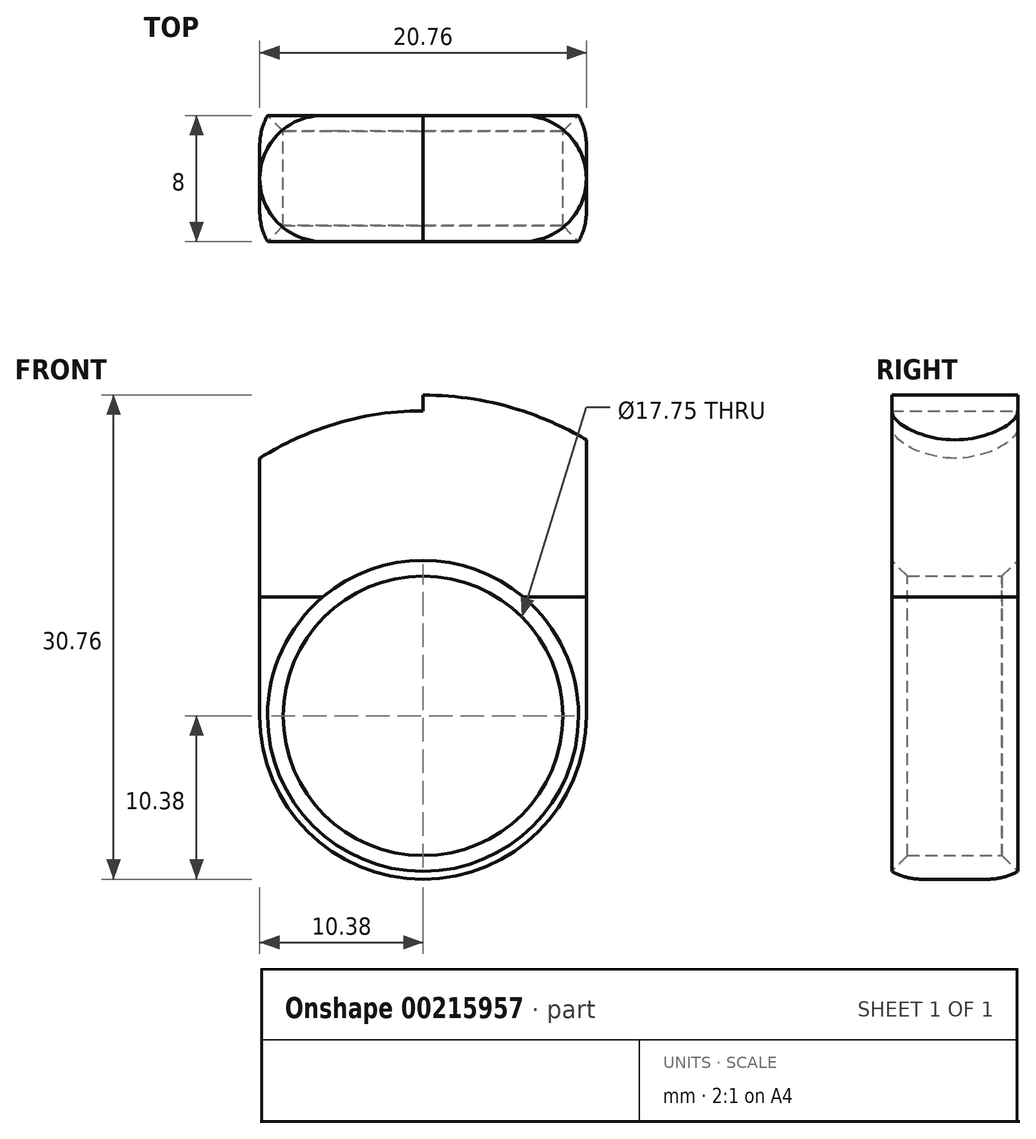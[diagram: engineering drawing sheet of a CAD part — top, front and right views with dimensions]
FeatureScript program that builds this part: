
annotation { "Feature Type Name" : "Feature", "Feature Type Description" : "" }
export const myFeature = defineFeature(function(context is Context, id is Id, definition is map)
    precondition{}
    {
        {
            var Q0;
            Q0=qCreatedBy(makeId("Front.planeOp"),FACE);
            var sketch = newSketch(context, id + "F0", { "sketchPlane" : qUnion([Q0])});
            skCircle(sketch, "E0", {"center": v(0, 0) * mm, "radius": 8.88 * mm});
            skCircle(sketch, "E1.0", {"center": v(0, 0) * mm, "radius": 10.38 * mm});
            skCircle(sketch, "E2.0", {"center": v(0, 0) * mm, "radius": 20.38 * mm});
            skLineSegment(sketch, "E3", {"start": v(10.38, 0) * mm, "end": v(10.38, 17.54) * mm});
            skLineSegment(sketch, "E4.MirrorCS", {"start": v(-10.38, 0) * mm, "end": v(-10.38, 17.54) * mm});
            skCircle(sketch, "E5.0", {"center": v(0, 0) * mm, "radius": 19.38 * mm});
            skLineSegment(sketch, "E6", {"start": v(-0.5, 20.37) * mm, "end": v(-0.5, 19.37) * mm});
            skLineSegment(sketch, "E7.MirrorCS", {"start": v(0.5, 20.37) * mm, "end": v(0.5, 19.37) * mm});
            skLineSegment(sketch, "E8", {"start": v(0, 20.38) * mm, "end": v(0, 19.38) * mm});
            skArc(sketch, "E9", {"start": v(10.37, 13.23) * mm, "mid": v(0, 16.81) * mm, "end": v(-10.37, 13.23) * mm});
            skLineSegment(sketch, "E10", {"start": v(0, 19.38) * mm, "end": v(0, 16.81) * mm});
            skSolve(sketch);
        }
        {
            var Q0;
            Q0=makeQuery(id+"F0.imprint","IMPRINT",FACE,{"disambiguationData":[TD([[makeQuery(id+"F0.imprint","IMPRINT",EDGE,{"derivedFrom":sQuery(id+"F0.wireOp",EDGE,"E0")}),-1.0]])]});
            extrude(context, id + "F1", {"entities" : qUnion([Q0]), "depth" : 4 * mm, "hasSecondDirection" : true, "secondDirectionOppositeDirection" : true, "secondDirectionDepth" : 4 * mm});
        }
        {
            var Q0;
            Q0=makeQuery(id+"F1.opExtrude","CAP_EDGE",EDGE,{"disambiguationData":[OSD([sQuery(id+"F0.wireOp",EDGE,"E0")])],"isStart":false});
            var Q1;
            Q1=makeQuery(id+"F1.opExtrude","CAP_EDGE",EDGE,{"disambiguationData":[OSD([sQuery(id+"F0.wireOp",EDGE,"E0")])],"isStart":true});
            chamfer(context, id + "F2", {"entities" : qUnion([Q0, Q1]), "width" : 1 * mm, "tangentPropagation" : true});
        }
        {
            var Q0;
            {var subQ0=sQuery(id+"F0.wireOp",EDGE,"E3");var subQ1=sQuery(id+"F0.wireOp",EDGE,"E1.0");var subQ2=makeQuery(id+"F0.imprint","INTERSECT",VERTEX,{"derivedFrom":[subQ1,subQ0]});Q0=makeQuery(id+"F0.imprint","IMPRINT",FACE,{"disambiguationData":[TD([[makeQuery(id+"F0.imprint","IMPRINT",EDGE,{"disambiguationData":[TD([[subQ2,-1.0]])],"derivedFrom":subQ1}),-1.0]])]});}
            var Q1;
            {var subQ0=sQuery(id+"F0.wireOp",EDGE,"E3");var subQ1=sQuery(id+"F0.wireOp",EDGE,"E2.0");var subQ2=makeQuery(id+"F0.imprint","INTERSECT",VERTEX,{"derivedFrom":[subQ1,subQ0]});Q1=makeQuery(id+"F0.imprint","IMPRINT",FACE,{"disambiguationData":[TD([[makeQuery(id+"F0.imprint","IMPRINT",EDGE,{"disambiguationData":[TD([[subQ2,-1.0]])],"derivedFrom":subQ1}),1.0]])]});}
            var Q2;
            {var subQ0=sQuery(id+"F0.wireOp",EDGE,"E7.MirrorCS");Q2=makeQuery(id+"F0.imprint","IMPRINT",FACE,{"disambiguationData":[TD([[makeQuery(id+"F0.imprint","IMPRINT",EDGE,{"derivedFrom":subQ0}),-1.0]])]});}
            var Q3;
            {var subQ3=sQuery(id+"F0.wireOp",EDGE,"E10");Q3=makeQuery(id+"F0.imprint","IMPRINT",FACE,{"disambiguationData":[TD([[makeQuery(id+"F0.imprint","IMPRINT",EDGE,{"derivedFrom":subQ3}),1.0]])]});}
            var Q4;
            {var subQ3=sQuery(id+"F0.wireOp",EDGE,"E10");Q4=makeQuery(id+"F0.imprint","IMPRINT",FACE,{"disambiguationData":[TD([[makeQuery(id+"F0.imprint","IMPRINT",EDGE,{"derivedFrom":subQ3}),-1.0]])]});}
            extrude(context, id + "F3", {"entities" : qUnion([Q0, Q1, Q2, Q3, Q4]), "operationType" : NewBodyOperationType.ADD, "depth" : 4 * mm, "hasSecondDirection" : true, "secondDirectionOppositeDirection" : true, "secondDirectionDepth" : 4 * mm});
        }
        {
            var Q0;
            Q0=makeQuery(id+"F3.opExtrude","CAP_EDGE",EDGE,{"disambiguationData":[OSD([sQuery(id+"F0.wireOp",EDGE,"E3")])],"isStart":false});
            var Q1;
            Q1=makeQuery(id+"F3.opExtrude","CAP_EDGE",EDGE,{"disambiguationData":[OSD([sQuery(id+"F0.wireOp",EDGE,"E3")])],"isStart":true});
            var Q2;
            Q2=makeQuery(id+"F3.opExtrude","CAP_EDGE",EDGE,{"disambiguationData":[OSD([sQuery(id+"F0.wireOp",EDGE,"E4.MirrorCS")])],"isStart":false});
            var Q3;
            Q3=makeQuery(id+"F3.opExtrude","CAP_EDGE",EDGE,{"disambiguationData":[OSD([sQuery(id+"F0.wireOp",EDGE,"E4.MirrorCS")])],"isStart":true});
            fillet(context, id + "F4", {"entities" : qUnion([Q0, Q1, Q2, Q3]), "radius" : 4 * mm, "tangentPropagation" : true, "allowEdgeOverflow" : false});
        }
    });
